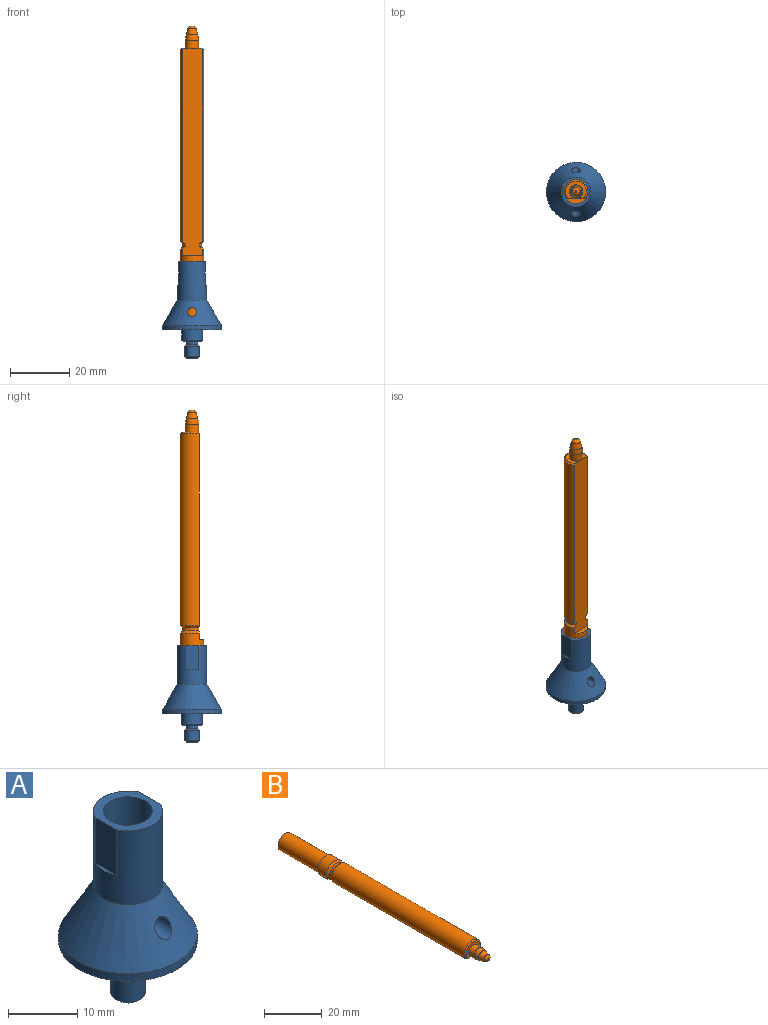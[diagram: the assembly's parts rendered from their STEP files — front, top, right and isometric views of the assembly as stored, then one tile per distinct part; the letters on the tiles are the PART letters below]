
ASSEMBLY  parts=2 mates=1
PART A: 22 faces, bbox 20x20x32.5 mm
  f0: plane 10x9mm, normal (0,0,1), area 36mm2, adj f1,f4,f18,f20
  f1: cylinder r=3.55mm len=20mm, axis (0,0,-1), area 431.6mm2, adj f0,f3,f13,f14
  f2: cone r=5mm half-angle=30deg, axis (0,0,-1), area 454.8mm2, adj f4,f5,f13,f14
  f3: plane 7.1x7.1mm, normal (0,0,1), area 39.6mm2, adj f1
  f4: cylinder r=5mm len=13mm, axis (0,0,-1), area 336.2mm2, adj f0,f2,f18,f19,f20,f21
  f5: cylinder r=10mm len=20mm, axis (0,0,-1), area 84.2mm2, adj f2,f6
  f6: plane 20x20mm, normal (0,0,-1), area 274.6mm2, adj f5,f7
  f7: cylinder r=3.55mm len=7.1mm, axis (0,0,-1), area 78.1mm2, adj f6,f17
  f8: plane 6.1x6.1mm, normal (0,0,-1), area 17mm2, adj f9,f17
  f9: cylinder r=1.98mm len=3.95mm, axis (0,0,-1), area 12.4mm2, adj f8,f10
  f10: plane 4x4mm, normal (0,0,1), area 0.3mm2, adj f9,f16
  f11: cylinder r=2.5mm len=5mm, axis (0,0,-1), area 55mm2, adj f15,f16
  f12: plane 4x4mm, normal (0,0,-1), area 12.6mm2, adj f15
  f13: cylinder r=1.5mm len=4.96mm, axis (0,1,0), area 36.2mm2, adj f1,f2
  f14: cylinder r=1.5mm len=4.96mm, axis (0,1,0), area 36.2mm2, adj f1,f2
  f15: cone r=2mm half-angle=45deg, axis (0,0,1), area 10mm2, adj f11,f12
  f16: cone r=2.5mm half-angle=45deg, axis (0,0,-1), area 10mm2, adj f10,f11
  f17: cone r=3.05mm half-angle=45deg, axis (0,0,1), area 14.7mm2, adj f7,f8
  f18: plane 8x4.36mm, normal (1,0,0), area 34.9mm2, adj f0,f4,f19
  f19: plane 4.36x0.5mm, normal (0,0,1), area 1.5mm2, adj f4,f18
  f20: plane 8x4.36mm, normal (-1,0,0), area 34.9mm2, adj f0,f4,f21
  f21: plane 4.36x0.5mm, normal (0,0,1), area 1.5mm2, adj f4,f20
PART B: 17 faces, bbox 8x99.5x8 mm
  f0: cylinder r=4mm len=8mm, axis (0,-1,0), area 89.3mm2, adj f1,f5,f9,f13
  f1: plane 70.03x6.64mm, normal (0,0,-1), area 459.4mm2, adj f0,f3,f4,f9,f10,f12,f13,f14
  f2: cylinder r=3.5mm len=20mm, axis (0,1,0), area 439.8mm2, adj f5,f11
  f3: cylinder r=4mm len=64.75mm, axis (0,-1,0), area 1123.1mm2, adj f1,f10,f14
  f4: plane 7x5.75mm, normal (0,-1,0), area 17.9mm2, adj f1,f8,f10
  f5: plane 8x8mm, normal (0,1,0), area 11.8mm2, adj f0,f2
  f6: plane 0.37x0.37mm, normal (0,-1,0), area 0.1mm2, adj f15
  f7: cone r=1.12mm half-angle=16.1deg, axis (0,1,0), area 22.6mm2, adj f15,f16
  f8: cylinder r=2.25mm len=4.5mm, axis (0,1,0), area 36.8mm2, adj f4,f16
  f9: plane 6.61x1.75mm, normal (0,-1,0), area 8.1mm2, adj f0,f1
  f10: cone r=3.5mm half-angle=45deg, axis (0,1,0), area 11.8mm2, adj f1,f3,f4
  f11: plane 7x7mm, normal (0,1,0), area 38.5mm2, adj f2
  f12: cylinder r=3.25mm len=6.5mm, axis (0,1,0), area 15.2mm2, adj f1,f13,f14
  f13: cone r=4mm half-angle=45deg, axis (0,1,0), area 17.2mm2, adj f0,f1,f12
  f14: cone r=3mm half-angle=45deg, axis (0,-1,0), area 17.2mm2, adj f1,f3,f12
  f15: torus R=0.18mm, axis (0,-1,0), area 9mm2, adj f6,f7
  f16: revolved ~4.5x4.5mm, area 53.2mm2, adj f7,f8
PLACE A t=(-15.55,-11.75,3.32)mm fixed
PLACE B rot(axis=(-1,-0.02,0.02),90deg) t=(-15.55,-11.75,-16.81)mm
MATE cylindrical B.f2 <-> A.f1  axis (0,0,-1) through (-15.55,-11.75,5.69)mm
